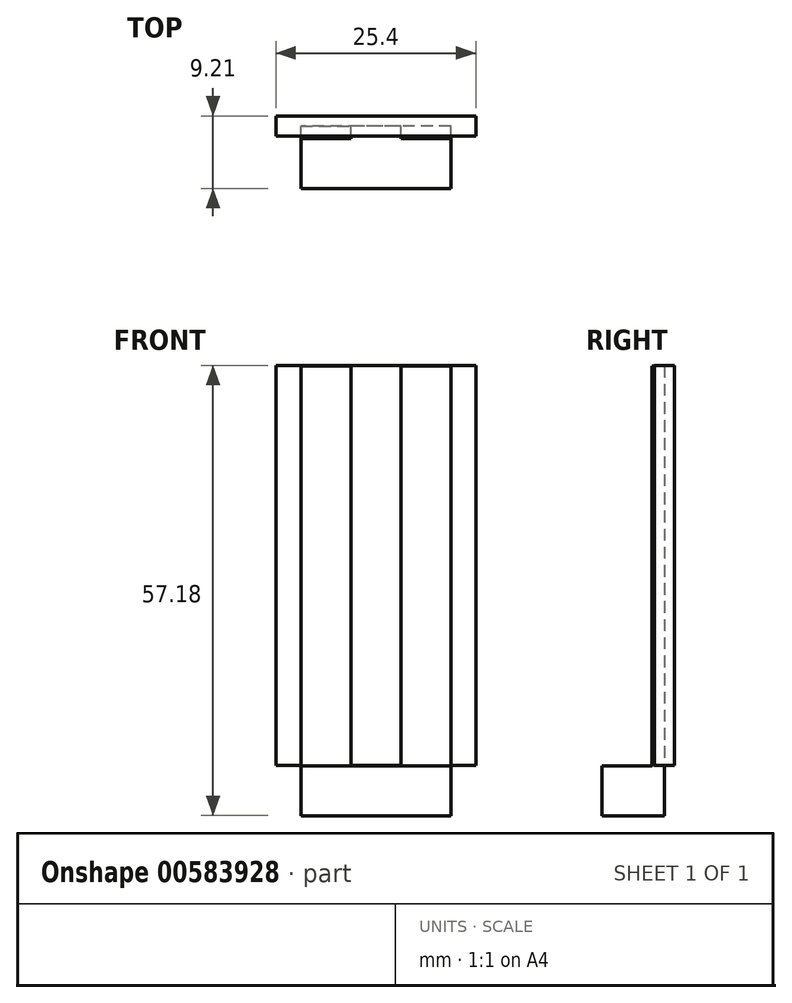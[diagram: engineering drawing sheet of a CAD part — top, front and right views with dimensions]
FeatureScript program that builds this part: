
annotation { "Feature Type Name" : "Feature", "Feature Type Description" : "" }
export const myFeature = defineFeature(function(context is Context, id is Id, definition is map)
    precondition{}
    {
        {
            var Q0;
            Q0=qCreatedBy(makeId("Top.planeOp"),FACE);
            var sketch = newSketch(context, id + "F0", { "sketchPlane" : qUnion([Q0])});
            skLineSegment(sketch, "E0.bottom", {"start": v(12.7, -1.27) * mm, "end": v(-12.7, -1.27) * mm});
            skLineSegment(sketch, "E0.top", {"start": v(12.7, 1.27) * mm, "end": v(-12.7, 1.27) * mm});
            skLineSegment(sketch, "E0.left", {"start": v(12.7, -1.27) * mm, "end": v(12.7, 1.27) * mm});
            skLineSegment(sketch, "E0.right", {"start": v(-12.7, -1.27) * mm, "end": v(-12.7, 1.27) * mm});
            skPoint(sketch, "E0.middle", {"position": v(0, 0) * mm});
            skSolve(sketch);
        }
        {
            var Q0;
            Q0 = qSketchRegion(id + "F0", true);
            extrude(context, id + "F1", {"entities" : qUnion([Q0]), "endBound" : BoundingType.SYMMETRIC, "depth" : 50.8 * mm, "offsetDistance" : 25.4 * mm});
        }
        {
            var Q0;
            Q0=qCreatedBy(makeId("Front.planeOp"),FACE);
            var sketch = newSketch(context, id + "F2", { "sketchPlane" : qUnion([Q0])});
            skPoint(sketch, "E1.middle", {"position": v(0, 0) * mm});
            skLineSegment(sketch, "E2", {"start": v(-9.53, 25.37) * mm, "end": v(-3.18, 25.37) * mm});
            skLineSegment(sketch, "E3", {"start": v(9.52, 25.37) * mm, "end": v(3.17, 25.37) * mm});
            skLineSegment(sketch, "E4", {"start": v(-9.53, 25.37) * mm, "end": v(-9.53, -25.43) * mm});
            skLineSegment(sketch, "E5", {"start": v(-3.18, -25.43) * mm, "end": v(-3.18, 25.37) * mm});
            skLineSegment(sketch, "E6", {"start": v(3.17, 25.37) * mm, "end": v(3.18, -25.43) * mm});
            skLineSegment(sketch, "E7", {"start": v(9.52, -25.43) * mm, "end": v(9.52, 25.37) * mm});
            skLineSegment(sketch, "E8", {"start": v(3.18, -25.43) * mm, "end": v(-3.18, -25.43) * mm});
            skLineSegment(sketch, "E9", {"start": v(9.52, -25.43) * mm, "end": v(9.52, -31.78) * mm});
            skLineSegment(sketch, "E10", {"start": v(9.52, -31.78) * mm, "end": v(-9.53, -31.78) * mm});
            skLineSegment(sketch, "E11", {"start": v(-9.53, -31.78) * mm, "end": v(-9.53, -25.43) * mm});
            skSolve(sketch);
        }
        {
            var Q0;
            Q0 = qSketchRegion(id + "F2", true);
            extrude(context, id + "F3", {"entities" : qUnion([Q0]), "depth" : 1.59 * mm, "offsetDistance" : 25.4 * mm});
        }
        {
            var Q0;
            Q0=makeQuery(id+"F3.opExtrude","CAP_FACE",FACE,{"disambiguationData":[OSD([sQuery(id+"F2.wireOp",EDGE,"E2"),sQuery(id+"F2.wireOp",EDGE,"E3"),sQuery(id+"F2.wireOp",EDGE,"E4"),sQuery(id+"F2.wireOp",EDGE,"E5"),sQuery(id+"F2.wireOp",EDGE,"E6"),sQuery(id+"F2.wireOp",EDGE,"E7"),sQuery(id+"F2.wireOp",EDGE,"E8"),sQuery(id+"F2.wireOp",EDGE,"E9"),sQuery(id+"F2.wireOp",EDGE,"E10"),sQuery(id+"F2.wireOp",EDGE,"E11")])],"isStart":false});
            var sketch = newSketch(context, id + "F4", { "sketchPlane" : qUnion([Q0])});
            skLineSegment(sketch, "E12.bottom", {"start": v(9.52, -31.78) * mm, "end": v(-9.53, -31.78) * mm});
            skLineSegment(sketch, "E12.top", {"start": v(9.52, -25.43) * mm, "end": v(-9.53, -25.43) * mm});
            skLineSegment(sketch, "E12.left", {"start": v(9.52, -31.78) * mm, "end": v(9.52, -25.43) * mm});
            skLineSegment(sketch, "E12.right", {"start": v(-9.53, -31.78) * mm, "end": v(-9.53, -25.43) * mm});
            skSolve(sketch);
        }
        {
            var Q0;
            Q0 = qSketchRegion(id + "F4", true);
            extrude(context, id + "F5", {"entities" : qUnion([Q0]), "operationType" : NewBodyOperationType.ADD, "depth" : 6.35 * mm, "offsetDistance" : 25.4 * mm});
        }
    });
